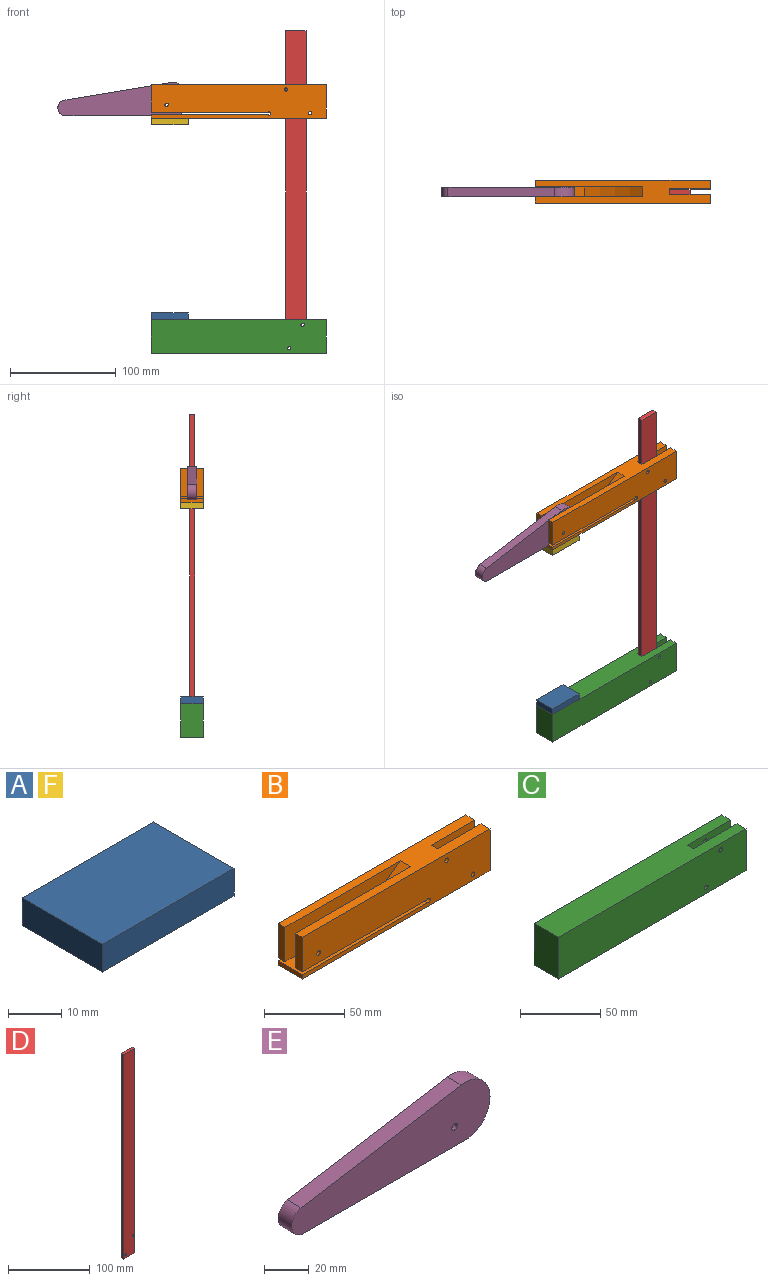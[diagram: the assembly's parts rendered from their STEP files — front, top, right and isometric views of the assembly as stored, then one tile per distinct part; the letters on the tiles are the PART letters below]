
ASSEMBLY  parts=6 mates=12
PART A: 6 faces, bbox 34.9x21.4x6.4 mm
  f0: plane 21.39x6.35mm, normal (-1,0,0), area 135.8mm2, adj f1,f3,f4,f5
  f1: plane 34.93x6.35mm, normal (0,-1,0), area 221.8mm2, adj f0,f2,f4,f5
  f2: plane 21.39x6.35mm, normal (1,0,0), area 135.8mm2, adj f1,f3,f4,f5
  f3: plane 34.93x6.35mm, normal (0,1,0), area 221.8mm2, adj f0,f2,f4,f5
  f4: plane 34.93x21.39mm, normal (0,0,1), area 746.9mm2, adj f0,f1,f2,f3
  f5: plane 34.93x21.39mm, normal (0,0,-1), area 746.9mm2, adj f0,f1,f2,f3
PART B: 24 faces, bbox 165.1x21.4x31.8 mm
  f0: plane 31.75x7.92mm, normal (1,0,0), area 251.3mm2, adj f1,f2,f4,f21
  f1: plane 165.1x21.39mm, normal (0,0,1), area 2391.9mm2, adj f0,f4,f5,f7,f8,f9,f10,f12
  f2: plane 165.1x21.39mm, normal (0,0,-1), area 3319.3mm2, adj f0,f4,f6,f8,f13,f20,f21,f22
  f3: cylinder r=1.59mm len=7.92mm, axis (0,-1,0), area 79mm2, adj f8,f20
  f4: plane 165.1x31.75mm, normal (0,1,0), area 4949mm2, adj f0,f1,f2,f6,f7,f11,f14,f15
  f5: cylinder r=127mm len=55.52mm, axis (0,1,0), area 566mm2, adj f1,f9,f10,f14
  f6: plane 21.39x3.18mm, normal (-1,0,0), area 67.9mm2, adj f2,f4,f8,f11
  f7: plane 26.19x6.13mm, normal (-1,0,0), area 160.6mm2, adj f1,f4,f10,f14
  f8: plane 165.1x31.75mm, normal (0,-1,0), area 4949mm2, adj f1,f2,f3,f6,f11,f12,f13,f14
  f9: plane 101.6x26.19mm, normal (0,1,0), area 2080.8mm2, adj f1,f5,f12,f14,f17
  f10: plane 101.6x26.19mm, normal (0,-1,0), area 2080.8mm2, adj f1,f5,f7,f14,f16
  f11: plane 110.08x21.39mm, normal (0,0,1), area 2354.2mm2, adj f4,f6,f8,f15
  f12: plane 26.19x6.13mm, normal (-1,0,0), area 160.6mm2, adj f1,f8,f9,f14
  f13: plane 31.75x7.92mm, normal (1,0,0), area 251.3mm2, adj f1,f2,f8,f20
  f14: plane 110.08x21.39mm, normal (0,0,-1), area 1933.6mm2, adj f4,f5,f7,f8,f9,f10,f12,f15
  f15: cylinder r=1.59mm len=21.39mm, axis (0,-1,0), area 155.7mm2, adj f4,f8,f11,f14
  f16: cylinder r=1.59mm len=6.13mm, axis (0,-1,0), area 61.1mm2, adj f4,f10
  f17: cylinder r=1.59mm len=6.13mm, axis (0,-1,0), area 61.1mm2, adj f8,f9
  f18: cylinder r=1.59mm len=7.92mm, axis (0,-1,0), area 79mm2, adj f4,f21
  f19: cylinder r=1.59mm len=21.39mm, axis (0,-1,0), area 185.6mm2, adj f4,f8,f20,f21,f22,f23
  f20: plane 38.1x31.75mm, normal (0,1,0), area 1197.8mm2, adj f1,f2,f3,f13,f19,f22,f23
  f21: plane 38.1x31.75mm, normal (0,-1,0), area 1197.8mm2, adj f0,f1,f2,f18,f19,f22,f23
  f22: plane 25.4x5.56mm, normal (1,0,0), area 141.1mm2, adj f2,f19,f20,f21
  f23: plane 5.56x3.18mm, normal (1,0,0), area 17.6mm2, adj f1,f19,f20,f21
PART C: 14 faces, bbox 165.1x21.4x31.8 mm
  f0: plane 31.75x7.92mm, normal (1,0,0), area 251.3mm2, adj f1,f2,f5,f7
  f1: plane 165.1x21.39mm, normal (0,0,-1), area 3319.3mm2, adj f0,f3,f4,f5,f6,f7,f8,f9
  f2: plane 165.1x21.39mm, normal (0,0,1), area 3319.3mm2, adj f0,f3,f4,f5,f6,f7,f8,f9
  f3: plane 31.75x21.39mm, normal (-1,0,0), area 679mm2, adj f1,f2,f5,f6
  f4: plane 31.75x7.92mm, normal (1,0,0), area 251.3mm2, adj f1,f2,f6,f8
  f5: plane 165.1x31.75mm, normal (0,-1,0), area 5226.1mm2, adj f0,f1,f2,f3,f12,f13
  f6: plane 165.1x31.75mm, normal (0,1,0), area 5226.1mm2, adj f1,f2,f3,f4,f10,f11
  f7: plane 38.1x31.75mm, normal (0,1,0), area 1193.8mm2, adj f0,f1,f2,f9,f12,f13
  f8: plane 38.1x31.75mm, normal (0,-1,0), area 1193.8mm2, adj f1,f2,f4,f9,f10,f11
  f9: plane 31.75x5.56mm, normal (1,0,0), area 176.4mm2, adj f1,f2,f7,f8
  f10: cylinder r=1.59mm len=7.92mm, axis (0,-1,0), area 79mm2, adj f6,f8
  f11: cylinder r=1.59mm len=7.92mm, axis (0,-1,0), area 79mm2, adj f6,f8
  f12: cylinder r=1.59mm len=7.92mm, axis (0,-1,0), area 79mm2, adj f5,f7
  f13: cylinder r=1.59mm len=7.92mm, axis (0,-1,0), area 79mm2, adj f5,f7
PART D: 8 faces, bbox 19.1x4.8x304.8 mm
  f0: plane 19.05x4.76mm, normal (0,0,1), area 90.7mm2, adj f1,f3,f4,f5
  f1: plane 304.8x4.76mm, normal (-1,0,0), area 1451.6mm2, adj f0,f2,f4,f5
  f2: plane 19.05x4.76mm, normal (0,0,-1), area 90.7mm2, adj f1,f3,f4,f5
  f3: plane 304.8x4.76mm, normal (1,0,0), area 1451.6mm2, adj f0,f2,f4,f5
  f4: plane 304.8x19.05mm, normal (0,-1,0), area 5790.6mm2, adj f0,f1,f2,f3,f6,f7
  f5: plane 304.8x19.05mm, normal (0,1,0), area 5790.6mm2, adj f0,f1,f2,f3,f6,f7
  f6: cylinder r=1.59mm len=4.76mm, axis (0,-1,0), area 47.5mm2, adj f4,f5
  f7: cylinder r=1.59mm len=4.76mm, axis (0,-1,0), area 47.5mm2, adj f4,f5
PART E: 7 faces, bbox 125.1x8.7x31.6 mm
  f0: plane 104.78x8.73mm, normal (0,0,-1), area 914.8mm2, adj f1,f3,f4,f5
  f1: cylinder r=15.91mm len=31.64mm, axis (0,1,0), area 436.3mm2, adj f0,f2,f4,f5
  f2: plane 101.01x16.62mm, normal (-0.16,0,0.99), area 893.8mm2, adj f1,f3,f4,f5
  f3: cylinder r=7.55mm len=14.85mm, axis (0,1,0), area 184.4mm2, adj f0,f2,f4,f5
  f4: plane 125.06x31.64mm, normal (0,-1,0), area 2863.5mm2, adj f0,f1,f2,f3,f6
  f5: plane 125.06x31.64mm, normal (0,1,0), area 2863.5mm2, adj f0,f1,f2,f3,f6
  f6: cylinder r=1.79mm len=8.73mm, axis (0,-1,0), area 98mm2, adj f4,f5
PART F: same geometry as A
PLACE A t=(-71.7,96.41,-44.56)mm
PLACE B t=(-6.61,100.98,161.47)mm
PLACE C t=(-6.61,107.11,-60.44)mm
PLACE D t=(48.23,98.4,-19.16)mm
PLACE E t=(-87.16,100.58,155.43)mm
PLACE F t=(-71.7,96.41,139.5)mm
MATE planar A.f1 <-> C.f5  axis (0,-1,0) through (-71.7,85.72,-41.39)mm
MATE planar A.f5 <-> C.f2  axis (0,0,-1) through (-71.7,96.41,-44.56)mm
MATE planar E.f4 <-> B.f9  axis (0,-1,0) through (-108.08,91.85,160.59)mm
MATE planar C.f3 <-> A.f0  axis (-1,0,0) through (-89.16,96.41,-60.44)mm
MATE cylindrical D.f6 <-> C.f10  axis (0,-1,0) through (41.01,96.02,-71.55)mm
MATE planar B.f2 <-> F.f4  axis (0,0,-1) through (-10.66,96.41,145.85)mm
MATE planar D.f4 <-> C.f7  axis (0,-1,0) through (47.36,93.64,76.46)mm
MATE planar B.f4 <-> F.f3  axis (0,1,0) through (-5.27,107.11,162.35)mm
MATE cylindrical E.f6 <-> B.f16  axis (0,-1,0) through (-74.87,91.85,158.55)mm
MATE planar F.f0 <-> B.f12  axis (-1,0,0) through (-89.16,96.41,142.67)mm
MATE planar B.f8 <-> C.f5  axis (0,-1,0) through (-5.27,85.72,162.35)mm
MATE planar C.f0 <-> B.f13  axis (1,0,0) through (75.94,85.72,-44.56)mm
